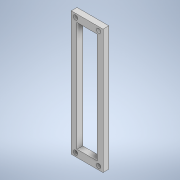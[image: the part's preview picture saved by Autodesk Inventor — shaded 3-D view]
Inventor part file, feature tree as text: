
AUTODESK INVENTOR PART (.ipt)
format: ipt  version: 2020.2 (Build 242310000, 310)  size: 124,928 bytes
history: native  units: mm
features: extrude x1, sketch x1
ambient origin geometry x8: Origin, YZ Plane, XZ Plane, XY Plane, X Axis, Y Axis, Z Axis, Center Point
bodies: Solid1 (feature_tree)
feature tree (2):
  extrude  "Extrusion1"  Depth=86.0mm
  sketch  "Sketch1"  dims[d0=22.0mm d1=86.0mm d2=3.0mm d3=3.0mm d4=3.0mm d5=3.0mm d6=3.0mm d7=2.5mm d8=3.0mm d9=2.5mm d10=2.5mm d11=3.0mm d12=3.0mm d13=2.5mm d14=14.0mm d15=76.0mm d16=4.0mm d17=0.0mm]
